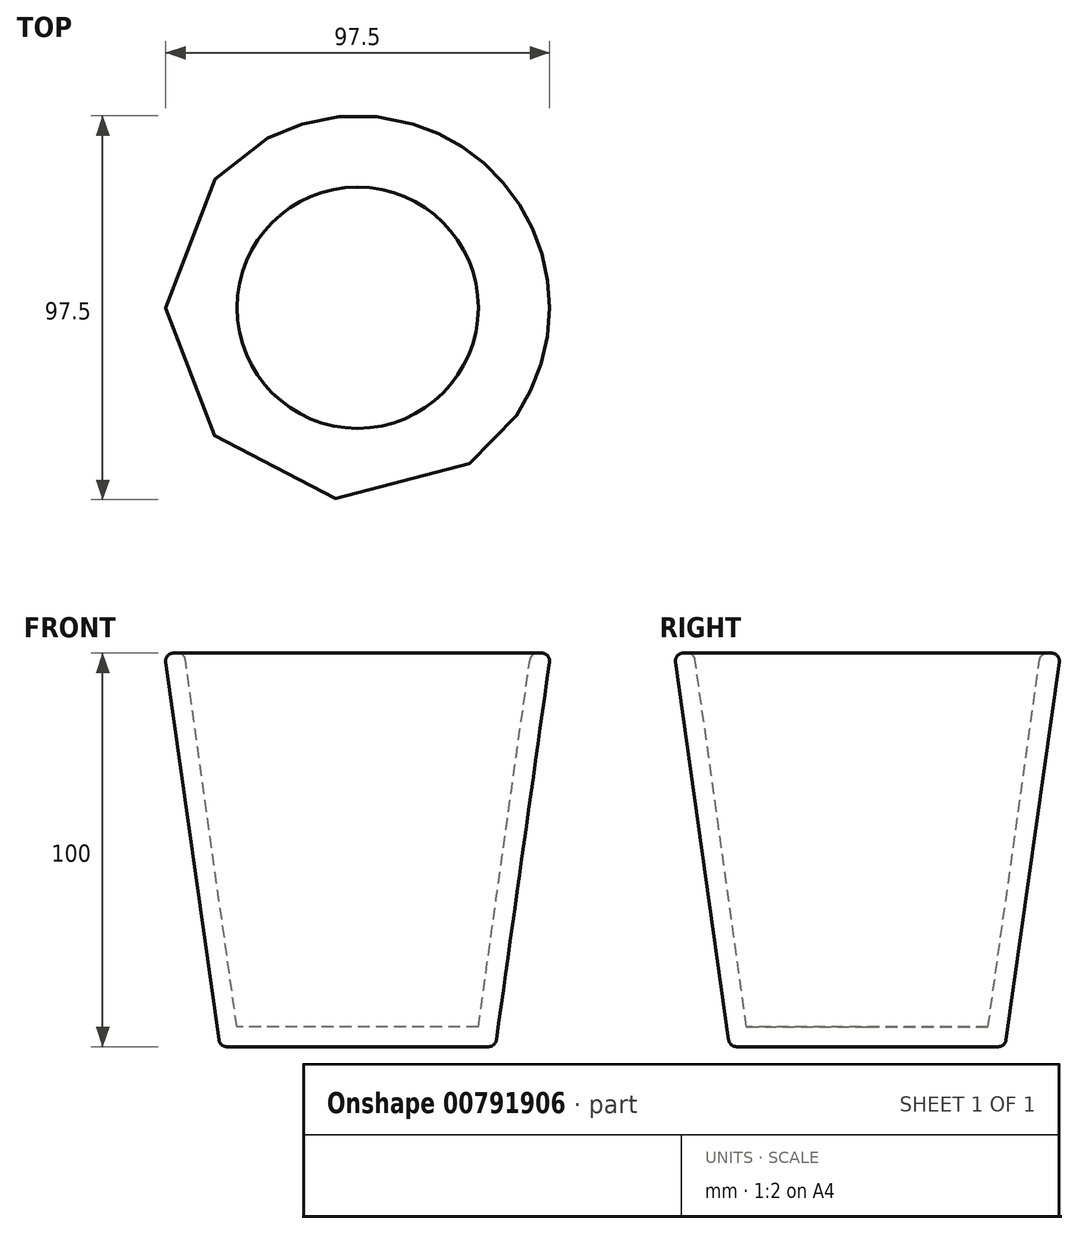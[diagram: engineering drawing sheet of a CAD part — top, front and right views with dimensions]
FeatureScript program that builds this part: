
annotation { "Feature Type Name" : "Feature", "Feature Type Description" : "" }
export const myFeature = defineFeature(function(context is Context, id is Id, definition is map)
    precondition{}
    {
        {
            var Q0;
            Q0=qCreatedBy(makeId("Top.planeOp"),FACE);
            var sketch = newSketch(context, id + "F0", { "sketchPlane" : qUnion([Q0])});
            skCircle(sketch, "E0", {"center": v(0, 0) * mm, "radius": 35 * mm});
            skSolve(sketch);
        }
        {
            var Q0;
            Q0 = qSketchRegion(id + "F0", true);
            extrude(context, id + "F1", {"entities" : qUnion([Q0]), "depth" : 100 * mm, "offsetDistance" : 25 * mm, "hasDraft" : true, "draftAngle" : 8 * degree});
        }
        {
            var Q0;
            Q0=makeQuery(id+"F1.opExtrude","CAP_FACE",FACE,{"disambiguationData":[OSD([sQuery(id+"F0.wireOp",EDGE,"E0")])],"isStart":false});
            shell(context, id + "F2", {"entities" : qUnion([Q0]), "thickness" : 5 * mm});
        }
        {
            var Q0;
            Q0=makeQuery(id+"F1.opExtrude","CAP_EDGE",EDGE,{"disambiguationData":[OSD([sQuery(id+"F0.wireOp",EDGE,"E0")])],"isStart":false});
            var Q1;
            {var subQ0=sQuery(id+"F0.wireOp",EDGE,"E0");Q1=makeQuery(id+"F2.opShell","OFFSET_EDGE",EDGE,{"disambiguationData":[OSD([subQ0]),TDD([makeQuery(id+"F1.opExtrude","CAP_EDGE",EDGE,{"disambiguationData":[OSD([subQ0])],"isStart":false})])]});}
            var Q2;
            Q2=makeQuery(id+"F1.opExtrude","CAP_EDGE",EDGE,{"disambiguationData":[OSD([sQuery(id+"F0.wireOp",EDGE,"E0")])],"isStart":true});
            fillet(context, id + "F3", {"entities" : qUnion([Q0, Q1, Q2]), "radius" : 2 * mm, "tangentPropagation" : true, "allowEdgeOverflow" : false});
        }
        {
            var Q0;
            Q0=qCreatedBy(makeId("Front.planeOp"),FACE);
            var sketch = newSketch(context, id + "F4", { "sketchPlane" : qUnion([Q0])});
            skLineSegment(sketch, "E1", {"start": v(48.96, 98.1) * mm, "end": v(34.91, 0) * mm, "construction": true});
            skFitSpline(sketch, "E2", {"points": [v(46.95, 84.12) * mm, v(86.57, 76.54) * mm, v(36.14, 8.6) * mm, v(35.92, 7.04) * mm], "startDerivative": vector(212.72, 162.39) * mm, "endDerivative": vector(19.49, 136.11) * mm});
            skSolve(sketch);
        }
        {
            var Q0;
            Q0=sQuery(id+"F4.wireOp",EDGE,"E2");
            var Q1;
            Q1=sQuery(id+"F4.wireOp",VERTEX,"E2.1.internal");
            cPlane(context, id + "F5", {"entities" : qUnion([Q0, Q1]), "cplaneType" : CPlaneType.CURVE_POINT, "offset" : 25 * mm, "width" : 150 * mm, "height" : 150 * mm});
        }
    });
